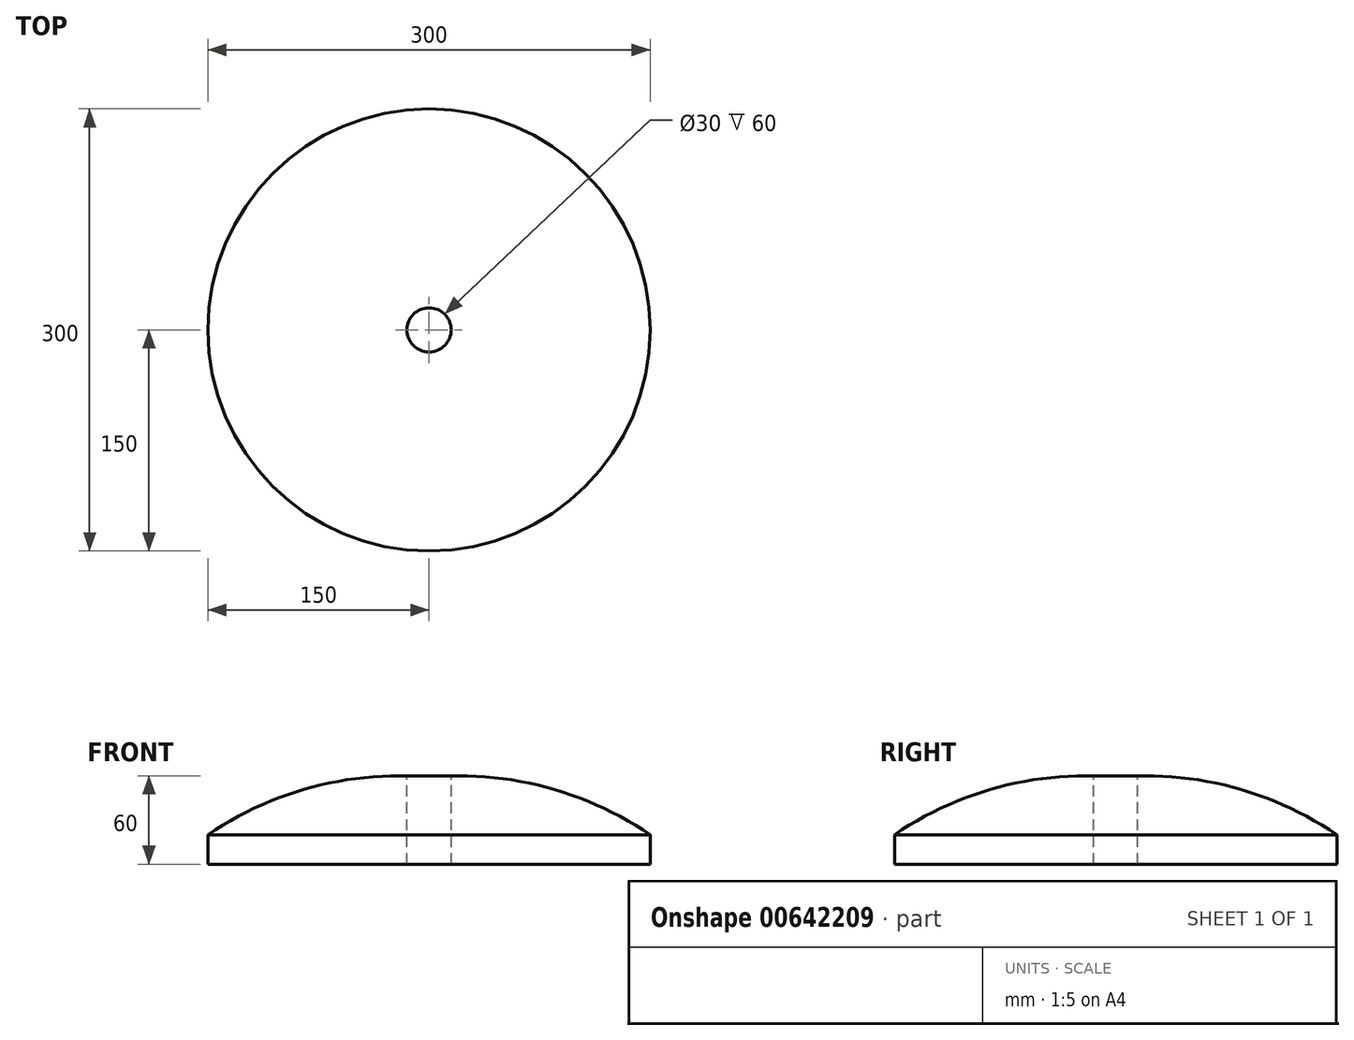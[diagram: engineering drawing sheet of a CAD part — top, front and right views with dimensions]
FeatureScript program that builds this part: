
annotation { "Feature Type Name" : "Feature", "Feature Type Description" : "" }
export const myFeature = defineFeature(function(context is Context, id is Id, definition is map)
    precondition{}
    {
        {
            var Q0;
            Q0=qCreatedBy(makeId("Front.planeOp"),FACE);
            var sketch = newSketch(context, id + "F0", { "sketchPlane" : qUnion([Q0])});
            skLineSegment(sketch, "E0", {"start": v(0, 0) * mm, "end": v(150, 0) * mm});
            skLineSegment(sketch, "E1", {"start": v(150, 0) * mm, "end": v(150, 20) * mm});
            skLineSegment(sketch, "E2", {"start": v(0, 0) * mm, "end": v(0, 60) * mm});
            skLineSegment(sketch, "E3", {"start": v(0, 60) * mm, "end": v(20, 60) * mm});
            skArc(sketch, "E4", {"start": v(150, 20) * mm, "mid": v(88, 49.77) * mm, "end": v(20, 60) * mm});
            skSolve(sketch);
        }
        {
            var Q0;
            Q0=makeQuery(id+"F0.imprint","IMPRINT",FACE,{"disambiguationData":[TD([[makeQuery(id+"F0.imprint","IMPRINT",EDGE,{"derivedFrom":sQuery(id+"F0.wireOp",EDGE,"E0")}),1.0]])]});
            var Q1;
            Q1=sQuery(id+"F0.wireOp",EDGE,"E2");
            revolve(context, id + "F1", {"entities" : qUnion([Q0]), "axis" : qUnion([Q1]), "revolveType" : RevolveType.FULL});
        }
        {
            var Q0;
            Q0=makeQuery(id+"F1.opRevolve","SWEPT_FACE",FACE,{"disambiguationData":[OSD([sQuery(id+"F0.wireOp",EDGE,"E3")])]});
            var sketch = newSketch(context, id + "F2", { "sketchPlane" : qUnion([Q0])});
            skCircle(sketch, "E5", {"center": v(0, 0) * mm, "radius": 15 * mm});
            skSolve(sketch);
        }
        {
            var Q0;
            Q0 = qSketchRegion(id + "F2", true);
            extrude(context, id + "F3", {"entities" : qUnion([Q0]), "operationType" : NewBodyOperationType.REMOVE, "oppositeDirection" : true, "depth" : 100 * mm, "offsetDistance" : 25 * mm});
        }
    });
